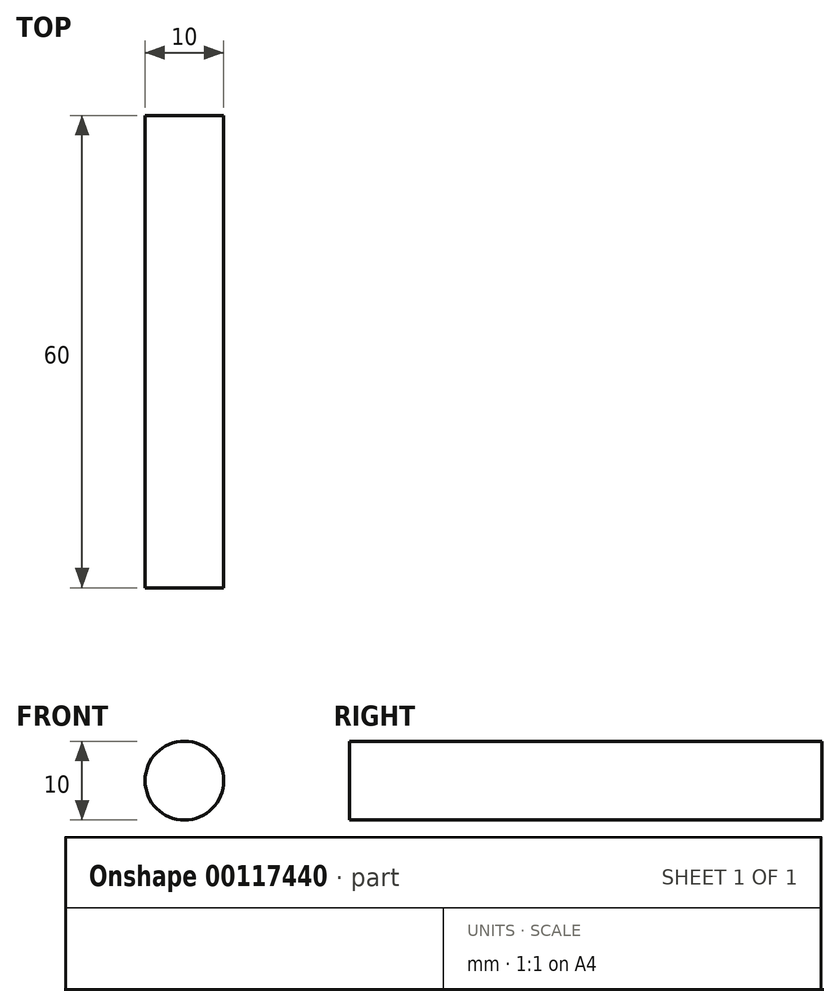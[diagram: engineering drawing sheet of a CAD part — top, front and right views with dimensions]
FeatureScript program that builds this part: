
annotation { "Feature Type Name" : "Feature", "Feature Type Description" : "" }
export const myFeature = defineFeature(function(context is Context, id is Id, definition is map)
    precondition{}
    {
        {
            var Q0;
            Q0=qCreatedBy(makeId("Front.planeOp"),FACE);
            var sketch = newSketch(context, id + "F0", { "sketchPlane" : qUnion([Q0])});
            skCircle(sketch, "E0", {"center": v(0, 0) * mm, "radius": 5 * mm});
            skSolve(sketch);
        }
        {
            var Q0;
            Q0=makeQuery(id+"F0.imprint","IMPRINT",FACE,{"disambiguationData":[TD([[makeQuery(id+"F0.imprint","IMPRINT",EDGE,{"derivedFrom":sQuery(id+"F0.wireOp",EDGE,"E0")}),1.0]])]});
            var Q1;
            Q1=sQuery(id+"F0.wireOp",EDGE,"E0");
            extrude(context, id + "F1", {"entities" : qUnion([Q0]), "surfaceEntities" : qUnion([Q1]), "depth" : 60 * mm});
        }
    });
